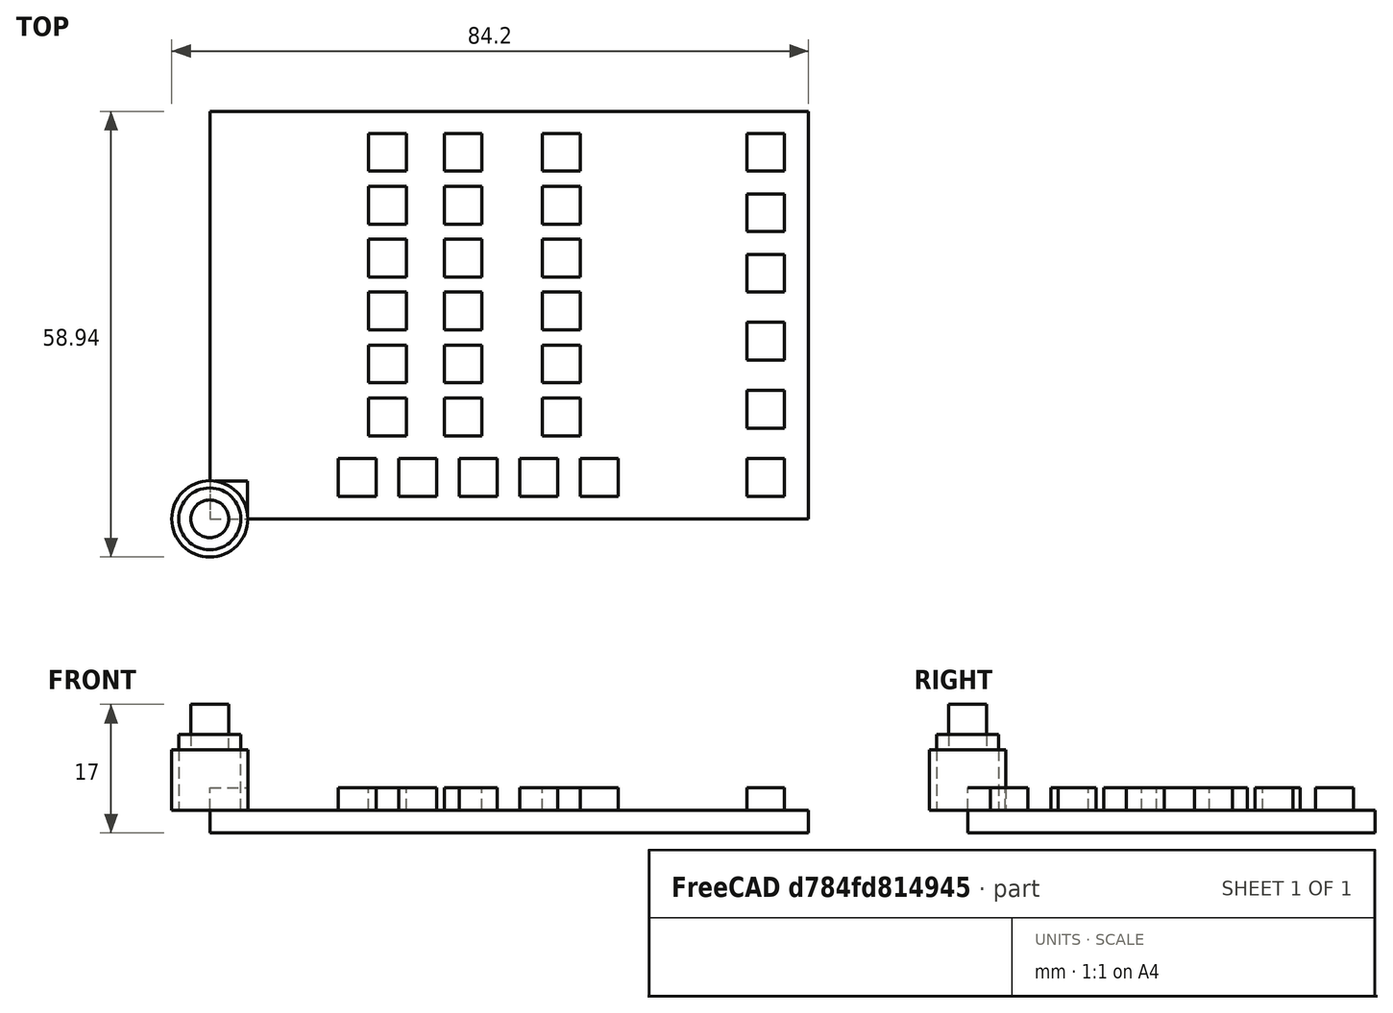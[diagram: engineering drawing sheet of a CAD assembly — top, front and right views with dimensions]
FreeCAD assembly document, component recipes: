
FREECAD ASSEMBLY — COMPONENT RECIPES ("PanelSchema")

This assembly document has 38 components, labeled P0..P37 below (a component is one placed body or linked part). 38 of them carry a construction recipe — the FreeCAD feature program that regenerates the part from scratch, quoted from this document or its linked companion documents; the rest are supplied as boundary geometry only. No exploded tour is included for this assembly.
COMPONENT P0 — recipe-attached ("Panel", modeled in this document).
Construction recipe (the document's own serialized feature program — sketch geometry with constraints, then the solid features built on it; lengths are millimeters unless a unit is written):

FEATURE [Sketcher::SketchObject] Sketch
  FullyConstrained = true
  MapMode = 5
  Support = -> [XY_Plane]
  sketch-geometry (4):
    g0: LineSegment StartX=0 StartY=0 StartZ=0 EndX=79.16 EndY=0 EndZ=0
    g1: LineSegment StartX=79.16 StartY=0 StartZ=0 EndX=79.16 EndY=53.9 EndZ=0
    g2: LineSegment StartX=79.16 StartY=53.9 StartZ=0 EndX=0 EndY=53.9 EndZ=0
    g3: LineSegment StartX=0 StartY=53.9 StartZ=0 EndX=0 EndY=0 EndZ=0
  constraints (11):
    c: Coincident(g0,g1)
    c: Coincident(g1,g2)
    c: Coincident(g2,g3)
    c: Coincident(g3,g0)
    c: Horizontal(g0)
    c: Horizontal(g2)
    c: Vertical(g1)
    c: Vertical(g3)
    c: Coincident(g0,g-1)
    c: DistanceX(g2,g2) = 79.16
    c: DistanceY(g3,g3) = 53.9
FEATURE [PartDesign::Pad] Pad
  Direction = (0,0,1)
  Length = 3
  Length2 = 10
  Profile = -> Sketch
  ReferenceAxis = -> Sketch [N_Axis]
  Type = 0
FEATURE [PartDesign::Body] Body  label="Panel"
  Group = -> [Sketch,Pad]
  Origin = -> Origin
  Tip = -> Pad
COMPONENT P1 — recipe-attached ("AP", modeled in this document).
Construction recipe (the document's own serialized feature program — sketch geometry with constraints, then the solid features built on it; lengths are millimeters unless a unit is written):

FEATURE [Sketcher::SketchObject] Sketch006
  FullyConstrained = true
  MapMode = 5
  Support = -> [XY_Plane004]
  sketch-geometry (4):
    g0: LineSegment StartX=0 StartY=0 StartZ=0 EndX=5 EndY=0 EndZ=0
    g1: LineSegment StartX=5 StartY=0 StartZ=0 EndX=5 EndY=5 EndZ=0
    g2: LineSegment StartX=5 StartY=5 StartZ=0 EndX=0 EndY=5 EndZ=0
    g3: LineSegment StartX=0 StartY=5 StartZ=0 EndX=0 EndY=0 EndZ=0
  constraints (11):
    c: Coincident(g0,g1)
    c: Coincident(g1,g2)
    c: Coincident(g2,g3)
    c: Coincident(g3,g0)
    c: Horizontal(g0)
    c: Horizontal(g2)
    c: Vertical(g1)
    c: Vertical(g3)
    c: Coincident(g0,g-1)
    c: DistanceY(g1,g1) = 5
    c: DistanceX(g2,g2) = 5
FEATURE [PartDesign::Pad] Pad005
  Direction = (0,0,1)
  Length = 3
  Length2 = 10
  Profile = -> Sketch006
  ReferenceAxis = -> Sketch006 [N_Axis]
  Type = 0
FEATURE [PartDesign::Body] Body004  label="AP"
  Group = -> [Sketch006,Pad005]
  Origin = -> Origin004
  Placement = pos=(21,46,3) rot=(0,0,1;0rad)
  Tip = -> Pad005
COMPONENT P2 — recipe-attached ("FD", modeled in this document).
Construction recipe (the document's own serialized feature program — sketch geometry with constraints, then the solid features built on it; lengths are millimeters unless a unit is written):

FEATURE [Sketcher::SketchObject] Sketch007
  FullyConstrained = true
  MapMode = 5
  Support = -> [XY_Plane005]
  sketch-geometry (4):
    g0: LineSegment StartX=0 StartY=0 StartZ=0 EndX=5 EndY=0 EndZ=0
    g1: LineSegment StartX=5 StartY=0 StartZ=0 EndX=5 EndY=5 EndZ=0
    g2: LineSegment StartX=5 StartY=5 StartZ=0 EndX=0 EndY=5 EndZ=0
    g3: LineSegment StartX=0 StartY=5 StartZ=0 EndX=0 EndY=0 EndZ=0
  constraints (11):
    c: Coincident(g0,g1)
    c: Coincident(g1,g2)
    c: Coincident(g2,g3)
    c: Coincident(g3,g0)
    c: Horizontal(g0)
    c: Horizontal(g2)
    c: Vertical(g1)
    c: Vertical(g3)
    c: Coincident(g0,g-1)
    c: DistanceY(g1,g1) = 5
    c: DistanceX(g2,g2) = 5
FEATURE [PartDesign::Pad] Pad006
  Direction = (0,0,1)
  Length = 3
  Length2 = 10
  Profile = -> Sketch007
  ReferenceAxis = -> Sketch007 [N_Axis]
  Type = 0
FEATURE [PartDesign::Body] Body005  label="FD"
  Group = -> [Sketch007,Pad006]
  Origin = -> Origin005
  Placement = pos=(21,39,3) rot=(0,0,1;0rad)
  Tip = -> Pad006
COMPONENT P3 — recipe-attached ("HDG", modeled in this document).
Construction recipe (the document's own serialized feature program — sketch geometry with constraints, then the solid features built on it; lengths are millimeters unless a unit is written):

FEATURE [Sketcher::SketchObject] Sketch008
  FullyConstrained = true
  MapMode = 5
  Support = -> [XY_Plane006]
  sketch-geometry (4):
    g0: LineSegment StartX=0 StartY=0 StartZ=0 EndX=5 EndY=0 EndZ=0
    g1: LineSegment StartX=5 StartY=0 StartZ=0 EndX=5 EndY=5 EndZ=0
    g2: LineSegment StartX=5 StartY=5 StartZ=0 EndX=0 EndY=5 EndZ=0
    g3: LineSegment StartX=0 StartY=5 StartZ=0 EndX=0 EndY=0 EndZ=0
  constraints (11):
    c: Coincident(g0,g1)
    c: Coincident(g1,g2)
    c: Coincident(g2,g3)
    c: Coincident(g3,g0)
    c: Horizontal(g0)
    c: Horizontal(g2)
    c: Vertical(g1)
    c: Vertical(g3)
    c: Coincident(g0,g-1)
    c: DistanceY(g1,g1) = 5
    c: DistanceX(g2,g2) = 5
FEATURE [PartDesign::Pad] Pad007
  Direction = (0,0,1)
  Length = 3
  Length2 = 10
  Profile = -> Sketch008
  ReferenceAxis = -> Sketch008 [N_Axis]
  Type = 0
FEATURE [PartDesign::Body] Body006  label="HDG"
  Group = -> [Sketch008,Pad007]
  Origin = -> Origin006
  Placement = pos=(21,32,3) rot=(0,0,1;0rad)
  Tip = -> Pad007
COMPONENT P4 — recipe-attached ("ALT", modeled in this document).
Construction recipe (the document's own serialized feature program — sketch geometry with constraints, then the solid features built on it; lengths are millimeters unless a unit is written):

FEATURE [Sketcher::SketchObject] Sketch009
  FullyConstrained = true
  MapMode = 5
  Support = -> [XY_Plane007]
  sketch-geometry (4):
    g0: LineSegment StartX=0 StartY=0 StartZ=0 EndX=5 EndY=0 EndZ=0
    g1: LineSegment StartX=5 StartY=0 StartZ=0 EndX=5 EndY=5 EndZ=0
    g2: LineSegment StartX=5 StartY=5 StartZ=0 EndX=0 EndY=5 EndZ=0
    g3: LineSegment StartX=0 StartY=5 StartZ=0 EndX=0 EndY=0 EndZ=0
  constraints (11):
    c: Coincident(g0,g1)
    c: Coincident(g1,g2)
    c: Coincident(g2,g3)
    c: Coincident(g3,g0)
    c: Horizontal(g0)
    c: Horizontal(g2)
    c: Vertical(g1)
    c: Vertical(g3)
    c: Coincident(g0,g-1)
    c: DistanceY(g1,g1) = 5
    c: DistanceX(g2,g2) = 5
FEATURE [PartDesign::Pad] Pad008
  Direction = (0,0,1)
  Length = 3
  Length2 = 10
  Profile = -> Sketch009
  ReferenceAxis = -> Sketch009 [N_Axis]
  Type = 0
FEATURE [PartDesign::Body] Body007  label="ALT"
  Group = -> [Sketch009,Pad008]
  Origin = -> Origin007
  Placement = pos=(21,25,3) rot=(0,0,1;0rad)
  Tip = -> Pad008
COMPONENT P5 — recipe-attached ("NAV", modeled in this document).
Construction recipe (the document's own serialized feature program — sketch geometry with constraints, then the solid features built on it; lengths are millimeters unless a unit is written):

FEATURE [Sketcher::SketchObject] Sketch010
  FullyConstrained = true
  MapMode = 5
  Support = -> [XY_Plane008]
  sketch-geometry (4):
    g0: LineSegment StartX=0 StartY=0 StartZ=0 EndX=5 EndY=0 EndZ=0
    g1: LineSegment StartX=5 StartY=0 StartZ=0 EndX=5 EndY=5 EndZ=0
    g2: LineSegment StartX=5 StartY=5 StartZ=0 EndX=0 EndY=5 EndZ=0
    g3: LineSegment StartX=0 StartY=5 StartZ=0 EndX=0 EndY=0 EndZ=0
  constraints (11):
    c: Coincident(g0,g1)
    c: Coincident(g1,g2)
    c: Coincident(g2,g3)
    c: Coincident(g3,g0)
    c: Horizontal(g0)
    c: Horizontal(g2)
    c: Vertical(g1)
    c: Vertical(g3)
    c: Coincident(g0,g-1)
    c: DistanceY(g1,g1) = 5
    c: DistanceX(g2,g2) = 5
FEATURE [PartDesign::Pad] Pad009
  Direction = (0,0,1)
  Length = 3
  Length2 = 10
  Profile = -> Sketch010
  ReferenceAxis = -> Sketch010 [N_Axis]
  Type = 0
FEATURE [PartDesign::Body] Body008  label="NAV"
  Group = -> [Sketch010,Pad009]
  Origin = -> Origin008
  Placement = pos=(21,18,3) rot=(0,0,1;0rad)
  Tip = -> Pad009
COMPONENT P6 — recipe-attached ("VNV", modeled in this document).
Construction recipe (the document's own serialized feature program — sketch geometry with constraints, then the solid features built on it; lengths are millimeters unless a unit is written):

FEATURE [Sketcher::SketchObject] Sketch011
  FullyConstrained = true
  MapMode = 5
  Support = -> [XY_Plane009]
  sketch-geometry (4):
    g0: LineSegment StartX=0 StartY=0 StartZ=0 EndX=5 EndY=0 EndZ=0
    g1: LineSegment StartX=5 StartY=0 StartZ=0 EndX=5 EndY=5 EndZ=0
    g2: LineSegment StartX=5 StartY=5 StartZ=0 EndX=0 EndY=5 EndZ=0
    g3: LineSegment StartX=0 StartY=5 StartZ=0 EndX=0 EndY=0 EndZ=0
  constraints (11):
    c: Coincident(g0,g1)
    c: Coincident(g1,g2)
    c: Coincident(g2,g3)
    c: Coincident(g3,g0)
    c: Horizontal(g0)
    c: Horizontal(g2)
    c: Vertical(g1)
    c: Vertical(g3)
    c: Coincident(g0,g-1)
    c: DistanceY(g1,g1) = 5
    c: DistanceX(g2,g2) = 5
FEATURE [PartDesign::Pad] Pad010
  Direction = (0,0,1)
  Length = 3
  Length2 = 10
  Profile = -> Sketch011
  ReferenceAxis = -> Sketch011 [N_Axis]
  Type = 0
FEATURE [PartDesign::Body] Body009  label="VNV"
  Group = -> [Sketch011,Pad010]
  Origin = -> Origin009
  Placement = pos=(21,11,3) rot=(0,0,1;0rad)
  Tip = -> Pad010
COMPONENT P7 — recipe-attached ("APR", modeled in this document).
Construction recipe (the document's own serialized feature program — sketch geometry with constraints, then the solid features built on it; lengths are millimeters unless a unit is written):

FEATURE [Sketcher::SketchObject] Sketch012
  FullyConstrained = true
  MapMode = 5
  Support = -> [XY_Plane010]
  sketch-geometry (4):
    g0: LineSegment StartX=0 StartY=0 StartZ=0 EndX=5 EndY=0 EndZ=0
    g1: LineSegment StartX=5 StartY=0 StartZ=0 EndX=5 EndY=5 EndZ=0
    g2: LineSegment StartX=5 StartY=5 StartZ=0 EndX=0 EndY=5 EndZ=0
    g3: LineSegment StartX=0 StartY=5 StartZ=0 EndX=0 EndY=0 EndZ=0
  constraints (11):
    c: Coincident(g0,g1)
    c: Coincident(g1,g2)
    c: Coincident(g2,g3)
    c: Coincident(g3,g0)
    c: Horizontal(g0)
    c: Horizontal(g2)
    c: Vertical(g1)
    c: Vertical(g3)
    c: Coincident(g0,g-1)
    c: DistanceY(g1,g1) = 5
    c: DistanceX(g2,g2) = 5
FEATURE [PartDesign::Pad] Pad011
  Direction = (0,0,1)
  Length = 3
  Length2 = 10
  Profile = -> Sketch012
  ReferenceAxis = -> Sketch012 [N_Axis]
  Type = 0
FEATURE [PartDesign::Body] Body010  label="APR"
  Group = -> [Sketch012,Pad011]
  Origin = -> Origin010
  Placement = pos=(31,46,3) rot=(0,0,1;0rad)
  Tip = -> Pad011
COMPONENT P8 — recipe-attached ("BC", modeled in this document).
Construction recipe (the document's own serialized feature program — sketch geometry with constraints, then the solid features built on it; lengths are millimeters unless a unit is written):

FEATURE [Sketcher::SketchObject] Sketch013
  FullyConstrained = true
  MapMode = 5
  Support = -> [XY_Plane011]
  sketch-geometry (4):
    g0: LineSegment StartX=0 StartY=0 StartZ=0 EndX=5 EndY=0 EndZ=0
    g1: LineSegment StartX=5 StartY=0 StartZ=0 EndX=5 EndY=5 EndZ=0
    g2: LineSegment StartX=5 StartY=5 StartZ=0 EndX=0 EndY=5 EndZ=0
    g3: LineSegment StartX=0 StartY=5 StartZ=0 EndX=0 EndY=0 EndZ=0
  constraints (11):
    c: Coincident(g0,g1)
    c: Coincident(g1,g2)
    c: Coincident(g2,g3)
    c: Coincident(g3,g0)
    c: Horizontal(g0)
    c: Horizontal(g2)
    c: Vertical(g1)
    c: Vertical(g3)
    c: Coincident(g0,g-1)
    c: DistanceY(g1,g1) = 5
    c: DistanceX(g2,g2) = 5
FEATURE [PartDesign::Pad] Pad012
  Direction = (0,0,1)
  Length = 3
  Length2 = 10
  Profile = -> Sketch013
  ReferenceAxis = -> Sketch013 [N_Axis]
  Type = 0
FEATURE [PartDesign::Body] Body011  label="BC"
  Group = -> [Sketch013,Pad012]
  Origin = -> Origin011
  Placement = pos=(31,39,3) rot=(0,0,1;0rad)
  Tip = -> Pad012
COMPONENT P9 — recipe-attached ("VS", modeled in this document).
Construction recipe (the document's own serialized feature program — sketch geometry with constraints, then the solid features built on it; lengths are millimeters unless a unit is written):

FEATURE [Sketcher::SketchObject] Sketch014
  FullyConstrained = true
  MapMode = 5
  Support = -> [XY_Plane012]
  sketch-geometry (4):
    g0: LineSegment StartX=0 StartY=0 StartZ=0 EndX=5 EndY=0 EndZ=0
    g1: LineSegment StartX=5 StartY=0 StartZ=0 EndX=5 EndY=5 EndZ=0
    g2: LineSegment StartX=5 StartY=5 StartZ=0 EndX=0 EndY=5 EndZ=0
    g3: LineSegment StartX=0 StartY=5 StartZ=0 EndX=0 EndY=0 EndZ=0
  constraints (11):
    c: Coincident(g0,g1)
    c: Coincident(g1,g2)
    c: Coincident(g2,g3)
    c: Coincident(g3,g0)
    c: Horizontal(g0)
    c: Horizontal(g2)
    c: Vertical(g1)
    c: Vertical(g3)
    c: Coincident(g0,g-1)
    c: DistanceY(g1,g1) = 5
    c: DistanceX(g2,g2) = 5
FEATURE [PartDesign::Pad] Pad013
  Direction = (0,0,1)
  Length = 3
  Length2 = 10
  Profile = -> Sketch014
  ReferenceAxis = -> Sketch014 [N_Axis]
  Type = 0
FEATURE [PartDesign::Body] Body012  label="VS"
  Group = -> [Sketch014,Pad013]
  Origin = -> Origin012
  Placement = pos=(31,32,3) rot=(0,0,1;0rad)
  Tip = -> Pad013
COMPONENT P10 — recipe-attached ("FLC", modeled in this document).
Construction recipe (the document's own serialized feature program — sketch geometry with constraints, then the solid features built on it; lengths are millimeters unless a unit is written):

FEATURE [Sketcher::SketchObject] Sketch015
  FullyConstrained = true
  MapMode = 5
  Support = -> [XY_Plane013]
  sketch-geometry (4):
    g0: LineSegment StartX=0 StartY=0 StartZ=0 EndX=5 EndY=0 EndZ=0
    g1: LineSegment StartX=5 StartY=0 StartZ=0 EndX=5 EndY=5 EndZ=0
    g2: LineSegment StartX=5 StartY=5 StartZ=0 EndX=0 EndY=5 EndZ=0
    g3: LineSegment StartX=0 StartY=5 StartZ=0 EndX=0 EndY=0 EndZ=0
  constraints (11):
    c: Coincident(g0,g1)
    c: Coincident(g1,g2)
    c: Coincident(g2,g3)
    c: Coincident(g3,g0)
    c: Horizontal(g0)
    c: Horizontal(g2)
    c: Vertical(g1)
    c: Vertical(g3)
    c: Coincident(g0,g-1)
    c: DistanceY(g1,g1) = 5
    c: DistanceX(g2,g2) = 5
FEATURE [PartDesign::Pad] Pad014
  Direction = (0,0,1)
  Length = 3
  Length2 = 10
  Profile = -> Sketch015
  ReferenceAxis = -> Sketch015 [N_Axis]
  Type = 0
FEATURE [PartDesign::Body] Body013  label="FLC"
  Group = -> [Sketch015,Pad014]
  Origin = -> Origin013
  Placement = pos=(31,25,3) rot=(0,0,1;0rad)
  Tip = -> Pad014
COMPONENT P11 — recipe-attached ("UP", modeled in this document).
Construction recipe (the document's own serialized feature program — sketch geometry with constraints, then the solid features built on it; lengths are millimeters unless a unit is written):

FEATURE [Sketcher::SketchObject] Sketch016
  FullyConstrained = true
  MapMode = 5
  Support = -> [XY_Plane014]
  sketch-geometry (4):
    g0: LineSegment StartX=0 StartY=0 StartZ=0 EndX=5 EndY=0 EndZ=0
    g1: LineSegment StartX=5 StartY=0 StartZ=0 EndX=5 EndY=5 EndZ=0
    g2: LineSegment StartX=5 StartY=5 StartZ=0 EndX=0 EndY=5 EndZ=0
    g3: LineSegment StartX=0 StartY=5 StartZ=0 EndX=0 EndY=0 EndZ=0
  constraints (11):
    c: Coincident(g0,g1)
    c: Coincident(g1,g2)
    c: Coincident(g2,g3)
    c: Coincident(g3,g0)
    c: Horizontal(g0)
    c: Horizontal(g2)
    c: Vertical(g1)
    c: Vertical(g3)
    c: Coincident(g0,g-1)
    c: DistanceY(g1,g1) = 5
    c: DistanceX(g2,g2) = 5
FEATURE [PartDesign::Pad] Pad015
  Direction = (0,0,1)
  Length = 3
  Length2 = 10
  Profile = -> Sketch016
  ReferenceAxis = -> Sketch016 [N_Axis]
  Type = 0
FEATURE [PartDesign::Body] Body014  label="UP"
  Group = -> [Sketch016,Pad015]
  Origin = -> Origin014
  Placement = pos=(31,18,3) rot=(0,0,1;0rad)
  Tip = -> Pad015
COMPONENT P12 — recipe-attached ("DN", modeled in this document).
Construction recipe (the document's own serialized feature program — sketch geometry with constraints, then the solid features built on it; lengths are millimeters unless a unit is written):

FEATURE [Sketcher::SketchObject] Sketch017
  FullyConstrained = true
  MapMode = 5
  Support = -> [XY_Plane015]
  sketch-geometry (4):
    g0: LineSegment StartX=0 StartY=0 StartZ=0 EndX=5 EndY=0 EndZ=0
    g1: LineSegment StartX=5 StartY=0 StartZ=0 EndX=5 EndY=5 EndZ=0
    g2: LineSegment StartX=5 StartY=5 StartZ=0 EndX=0 EndY=5 EndZ=0
    g3: LineSegment StartX=0 StartY=5 StartZ=0 EndX=0 EndY=0 EndZ=0
  constraints (11):
    c: Coincident(g0,g1)
    c: Coincident(g1,g2)
    c: Coincident(g2,g3)
    c: Coincident(g3,g0)
    c: Horizontal(g0)
    c: Horizontal(g2)
    c: Vertical(g1)
    c: Vertical(g3)
    c: Coincident(g0,g-1)
    c: DistanceY(g1,g1) = 5
    c: DistanceX(g2,g2) = 5
FEATURE [PartDesign::Pad] Pad016
  Direction = (0,0,1)
  Length = 3
  Length2 = 10
  Profile = -> Sketch017
  ReferenceAxis = -> Sketch017 [N_Axis]
  Type = 0
FEATURE [PartDesign::Body] Body015  label="DN"
  Group = -> [Sketch017,Pad016]
  Origin = -> Origin015
  Placement = pos=(31,11,3) rot=(0,0,1;0rad)
  Tip = -> Pad016
COMPONENT P13 — recipe-attached ("DCT", modeled in this document).
Construction recipe (the document's own serialized feature program — sketch geometry with constraints, then the solid features built on it; lengths are millimeters unless a unit is written):

FEATURE [Sketcher::SketchObject] Sketch018
  FullyConstrained = true
  MapMode = 5
  Support = -> [XY_Plane016]
  sketch-geometry (4):
    g0: LineSegment StartX=0 StartY=0 StartZ=0 EndX=5 EndY=0 EndZ=0
    g1: LineSegment StartX=5 StartY=0 StartZ=0 EndX=5 EndY=5 EndZ=0
    g2: LineSegment StartX=5 StartY=5 StartZ=0 EndX=0 EndY=5 EndZ=0
    g3: LineSegment StartX=0 StartY=5 StartZ=0 EndX=0 EndY=0 EndZ=0
  constraints (11):
    c: Coincident(g0,g1)
    c: Coincident(g1,g2)
    c: Coincident(g2,g3)
    c: Coincident(g3,g0)
    c: Horizontal(g0)
    c: Horizontal(g2)
    c: Vertical(g1)
    c: Vertical(g3)
    c: Coincident(g0,g-1)
    c: DistanceY(g1,g1) = 5
    c: DistanceX(g2,g2) = 5
FEATURE [PartDesign::Pad] Pad017
  Direction = (0,0,1)
  Length = 3
  Length2 = 10
  Profile = -> Sketch018
  ReferenceAxis = -> Sketch018 [N_Axis]
  Type = 0
FEATURE [PartDesign::Body] Body016  label="DCT"
  Group = -> [Sketch018,Pad017]
  Origin = -> Origin016
  Placement = pos=(44,46,3) rot=(0,0,1;0rad)
  Tip = -> Pad017
COMPONENT P14 — recipe-attached ("MNU", modeled in this document).
Construction recipe (the document's own serialized feature program — sketch geometry with constraints, then the solid features built on it; lengths are millimeters unless a unit is written):

FEATURE [Sketcher::SketchObject] Sketch019
  FullyConstrained = true
  MapMode = 5
  Support = -> [XY_Plane017]
  sketch-geometry (4):
    g0: LineSegment StartX=0 StartY=0 StartZ=0 EndX=5 EndY=0 EndZ=0
    g1: LineSegment StartX=5 StartY=0 StartZ=0 EndX=5 EndY=5 EndZ=0
    g2: LineSegment StartX=5 StartY=5 StartZ=0 EndX=0 EndY=5 EndZ=0
    g3: LineSegment StartX=0 StartY=5 StartZ=0 EndX=0 EndY=0 EndZ=0
  constraints (11):
    c: Coincident(g0,g1)
    c: Coincident(g1,g2)
    c: Coincident(g2,g3)
    c: Coincident(g3,g0)
    c: Horizontal(g0)
    c: Horizontal(g2)
    c: Vertical(g1)
    c: Vertical(g3)
    c: Coincident(g0,g-1)
    c: DistanceY(g1,g1) = 5
    c: DistanceX(g2,g2) = 5
FEATURE [PartDesign::Pad] Pad018
  Direction = (0,0,1)
  Length = 3
  Length2 = 10
  Profile = -> Sketch019
  ReferenceAxis = -> Sketch019 [N_Axis]
  Type = 0
FEATURE [PartDesign::Body] Body017  label="MNU"
  Group = -> [Sketch019,Pad018]
  Origin = -> Origin017
  Placement = pos=(44,39,3) rot=(0,0,1;0rad)
  Tip = -> Pad018
COMPONENT P15 — recipe-attached ("FPL", modeled in this document).
Construction recipe (the document's own serialized feature program — sketch geometry with constraints, then the solid features built on it; lengths are millimeters unless a unit is written):

FEATURE [Sketcher::SketchObject] Sketch020
  FullyConstrained = true
  MapMode = 5
  Support = -> [XY_Plane018]
  sketch-geometry (4):
    g0: LineSegment StartX=0 StartY=0 StartZ=0 EndX=5 EndY=0 EndZ=0
    g1: LineSegment StartX=5 StartY=0 StartZ=0 EndX=5 EndY=5 EndZ=0
    g2: LineSegment StartX=5 StartY=5 StartZ=0 EndX=0 EndY=5 EndZ=0
    g3: LineSegment StartX=0 StartY=5 StartZ=0 EndX=0 EndY=0 EndZ=0
  constraints (11):
    c: Coincident(g0,g1)
    c: Coincident(g1,g2)
    c: Coincident(g2,g3)
    c: Coincident(g3,g0)
    c: Horizontal(g0)
    c: Horizontal(g2)
    c: Vertical(g1)
    c: Vertical(g3)
    c: Coincident(g0,g-1)
    c: DistanceY(g1,g1) = 5
    c: DistanceX(g2,g2) = 5
FEATURE [PartDesign::Pad] Pad019
  Direction = (0,0,1)
  Length = 3
  Length2 = 10
  Profile = -> Sketch020
  ReferenceAxis = -> Sketch020 [N_Axis]
  Type = 0
FEATURE [PartDesign::Body] Body018  label="FPL"
  Group = -> [Sketch020,Pad019]
  Origin = -> Origin018
  Placement = pos=(44,32,3) rot=(0,0,1;0rad)
  Tip = -> Pad019
COMPONENT P16 — recipe-attached ("PROC", modeled in this document).
Construction recipe (the document's own serialized feature program — sketch geometry with constraints, then the solid features built on it; lengths are millimeters unless a unit is written):

FEATURE [Sketcher::SketchObject] Sketch021
  FullyConstrained = true
  MapMode = 5
  Support = -> [XY_Plane019]
  sketch-geometry (4):
    g0: LineSegment StartX=0 StartY=0 StartZ=0 EndX=5 EndY=0 EndZ=0
    g1: LineSegment StartX=5 StartY=0 StartZ=0 EndX=5 EndY=5 EndZ=0
    g2: LineSegment StartX=5 StartY=5 StartZ=0 EndX=0 EndY=5 EndZ=0
    g3: LineSegment StartX=0 StartY=5 StartZ=0 EndX=0 EndY=0 EndZ=0
  constraints (11):
    c: Coincident(g0,g1)
    c: Coincident(g1,g2)
    c: Coincident(g2,g3)
    c: Coincident(g3,g0)
    c: Horizontal(g0)
    c: Horizontal(g2)
    c: Vertical(g1)
    c: Vertical(g3)
    c: Coincident(g0,g-1)
    c: DistanceY(g1,g1) = 5
    c: DistanceX(g2,g2) = 5
FEATURE [PartDesign::Pad] Pad020
  Direction = (0,0,1)
  Length = 3
  Length2 = 10
  Profile = -> Sketch021
  ReferenceAxis = -> Sketch021 [N_Axis]
  Type = 0
FEATURE [PartDesign::Body] Body019  label="PROC"
  Group = -> [Sketch021,Pad020]
  Origin = -> Origin019
  Placement = pos=(44,25,3) rot=(0,0,1;0rad)
  Tip = -> Pad020
COMPONENT P17 — recipe-attached ("CLR", modeled in this document).
Construction recipe (the document's own serialized feature program — sketch geometry with constraints, then the solid features built on it; lengths are millimeters unless a unit is written):

FEATURE [Sketcher::SketchObject] Sketch022
  FullyConstrained = true
  MapMode = 5
  Support = -> [XY_Plane020]
  sketch-geometry (4):
    g0: LineSegment StartX=0 StartY=0 StartZ=0 EndX=5 EndY=0 EndZ=0
    g1: LineSegment StartX=5 StartY=0 StartZ=0 EndX=5 EndY=5 EndZ=0
    g2: LineSegment StartX=5 StartY=5 StartZ=0 EndX=0 EndY=5 EndZ=0
    g3: LineSegment StartX=0 StartY=5 StartZ=0 EndX=0 EndY=0 EndZ=0
  constraints (11):
    c: Coincident(g0,g1)
    c: Coincident(g1,g2)
    c: Coincident(g2,g3)
    c: Coincident(g3,g0)
    c: Horizontal(g0)
    c: Horizontal(g2)
    c: Vertical(g1)
    c: Vertical(g3)
    c: Coincident(g0,g-1)
    c: DistanceY(g1,g1) = 5
    c: DistanceX(g2,g2) = 5
FEATURE [PartDesign::Pad] Pad021
  Direction = (0,0,1)
  Length = 3
  Length2 = 10
  Profile = -> Sketch022
  ReferenceAxis = -> Sketch022 [N_Axis]
  Type = 0
FEATURE [PartDesign::Body] Body020  label="CLR"
  Group = -> [Sketch022,Pad021]
  Origin = -> Origin020
  Placement = pos=(44,18,3) rot=(0,0,1;0rad)
  Tip = -> Pad021
COMPONENT P18 — recipe-attached ("ENT", modeled in this document).
Construction recipe (the document's own serialized feature program — sketch geometry with constraints, then the solid features built on it; lengths are millimeters unless a unit is written):

FEATURE [Sketcher::SketchObject] Sketch023
  FullyConstrained = true
  MapMode = 5
  Support = -> [XY_Plane021]
  sketch-geometry (4):
    g0: LineSegment StartX=0 StartY=0 StartZ=0 EndX=5 EndY=0 EndZ=0
    g1: LineSegment StartX=5 StartY=0 StartZ=0 EndX=5 EndY=5 EndZ=0
    g2: LineSegment StartX=5 StartY=5 StartZ=0 EndX=0 EndY=5 EndZ=0
    g3: LineSegment StartX=0 StartY=5 StartZ=0 EndX=0 EndY=0 EndZ=0
  constraints (11):
    c: Coincident(g0,g1)
    c: Coincident(g1,g2)
    c: Coincident(g2,g3)
    c: Coincident(g3,g0)
    c: Horizontal(g0)
    c: Horizontal(g2)
    c: Vertical(g1)
    c: Vertical(g3)
    c: Coincident(g0,g-1)
    c: DistanceY(g1,g1) = 5
    c: DistanceX(g2,g2) = 5
FEATURE [PartDesign::Pad] Pad022
  Direction = (0,0,1)
  Length = 3
  Length2 = 10
  Profile = -> Sketch023
  ReferenceAxis = -> Sketch023 [N_Axis]
  Type = 0
FEATURE [PartDesign::Body] Body021  label="ENT"
  Group = -> [Sketch023,Pad022]
  Origin = -> Origin021
  Placement = pos=(44,11,3) rot=(0,0,1;0rad)
  Tip = -> Pad022
COMPONENT P19 — recipe-attached ("SW1", modeled in this document).
Construction recipe (the document's own serialized feature program — sketch geometry with constraints, then the solid features built on it; lengths are millimeters unless a unit is written):

FEATURE [Sketcher::SketchObject] Sketch024
  FullyConstrained = true
  MapMode = 5
  Support = -> [XY_Plane022]
  sketch-geometry (4):
    g0: LineSegment StartX=0 StartY=0 StartZ=0 EndX=5 EndY=0 EndZ=0
    g1: LineSegment StartX=5 StartY=0 StartZ=0 EndX=5 EndY=5 EndZ=0
    g2: LineSegment StartX=5 StartY=5 StartZ=0 EndX=0 EndY=5 EndZ=0
    g3: LineSegment StartX=0 StartY=5 StartZ=0 EndX=0 EndY=0 EndZ=0
  constraints (11):
    c: Coincident(g0,g1)
    c: Coincident(g1,g2)
    c: Coincident(g2,g3)
    c: Coincident(g3,g0)
    c: Horizontal(g0)
    c: Horizontal(g2)
    c: Vertical(g1)
    c: Vertical(g3)
    c: Coincident(g0,g-1)
    c: DistanceY(g1,g1) = 5
    c: DistanceX(g2,g2) = 5
FEATURE [PartDesign::Pad] Pad023
  Direction = (0,0,1)
  Length = 3
  Length2 = 10
  Profile = -> Sketch024
  ReferenceAxis = -> Sketch024 [N_Axis]
  Type = 0
FEATURE [PartDesign::Body] Body022  label="SW1"
  Group = -> [Sketch024,Pad023]
  Origin = -> Origin022
  Placement = pos=(17,3,3) rot=(0,0,1;0rad)
  Tip = -> Pad023
COMPONENT P20 — recipe-attached ("SW2", modeled in this document).
Construction recipe (the document's own serialized feature program — sketch geometry with constraints, then the solid features built on it; lengths are millimeters unless a unit is written):

FEATURE [Sketcher::SketchObject] Sketch025
  FullyConstrained = true
  MapMode = 5
  Support = -> [XY_Plane023]
  sketch-geometry (4):
    g0: LineSegment StartX=0 StartY=0 StartZ=0 EndX=5 EndY=0 EndZ=0
    g1: LineSegment StartX=5 StartY=0 StartZ=0 EndX=5 EndY=5 EndZ=0
    g2: LineSegment StartX=5 StartY=5 StartZ=0 EndX=0 EndY=5 EndZ=0
    g3: LineSegment StartX=0 StartY=5 StartZ=0 EndX=0 EndY=0 EndZ=0
  constraints (11):
    c: Coincident(g0,g1)
    c: Coincident(g1,g2)
    c: Coincident(g2,g3)
    c: Coincident(g3,g0)
    c: Horizontal(g0)
    c: Horizontal(g2)
    c: Vertical(g1)
    c: Vertical(g3)
    c: Coincident(g0,g-1)
    c: DistanceY(g1,g1) = 5
    c: DistanceX(g2,g2) = 5
FEATURE [PartDesign::Pad] Pad024
  Direction = (0,0,1)
  Length = 3
  Length2 = 10
  Profile = -> Sketch025
  ReferenceAxis = -> Sketch025 [N_Axis]
  Type = 0
FEATURE [PartDesign::Body] Body023  label="SW2"
  Group = -> [Sketch025,Pad024]
  Origin = -> Origin023
  Placement = pos=(25,3,3) rot=(0,0,1;0rad)
  Tip = -> Pad024
COMPONENT P21 — recipe-attached ("SW3", modeled in this document).
Construction recipe (the document's own serialized feature program — sketch geometry with constraints, then the solid features built on it; lengths are millimeters unless a unit is written):

FEATURE [Sketcher::SketchObject] Sketch026
  FullyConstrained = true
  MapMode = 5
  Support = -> [XY_Plane024]
  sketch-geometry (4):
    g0: LineSegment StartX=0 StartY=0 StartZ=0 EndX=5 EndY=0 EndZ=0
    g1: LineSegment StartX=5 StartY=0 StartZ=0 EndX=5 EndY=5 EndZ=0
    g2: LineSegment StartX=5 StartY=5 StartZ=0 EndX=0 EndY=5 EndZ=0
    g3: LineSegment StartX=0 StartY=5 StartZ=0 EndX=0 EndY=0 EndZ=0
  constraints (11):
    c: Coincident(g0,g1)
    c: Coincident(g1,g2)
    c: Coincident(g2,g3)
    c: Coincident(g3,g0)
    c: Horizontal(g0)
    c: Horizontal(g2)
    c: Vertical(g1)
    c: Vertical(g3)
    c: Coincident(g0,g-1)
    c: DistanceY(g1,g1) = 5
    c: DistanceX(g2,g2) = 5
FEATURE [PartDesign::Pad] Pad025
  Direction = (0,0,1)
  Length = 3
  Length2 = 10
  Profile = -> Sketch026
  ReferenceAxis = -> Sketch026 [N_Axis]
  Type = 0
FEATURE [PartDesign::Body] Body024  label="SW3"
  Group = -> [Sketch026,Pad025]
  Origin = -> Origin024
  Placement = pos=(33,3,3) rot=(0,0,1;0rad)
  Tip = -> Pad025
COMPONENT P22 — recipe-attached ("SW4", modeled in this document).
Construction recipe (the document's own serialized feature program — sketch geometry with constraints, then the solid features built on it; lengths are millimeters unless a unit is written):

FEATURE [Sketcher::SketchObject] Sketch027
  FullyConstrained = true
  MapMode = 5
  Support = -> [XY_Plane025]
  sketch-geometry (4):
    g0: LineSegment StartX=0 StartY=0 StartZ=0 EndX=5 EndY=0 EndZ=0
    g1: LineSegment StartX=5 StartY=0 StartZ=0 EndX=5 EndY=5 EndZ=0
    g2: LineSegment StartX=5 StartY=5 StartZ=0 EndX=0 EndY=5 EndZ=0
    g3: LineSegment StartX=0 StartY=5 StartZ=0 EndX=0 EndY=0 EndZ=0
  constraints (11):
    c: Coincident(g0,g1)
    c: Coincident(g1,g2)
    c: Coincident(g2,g3)
    c: Coincident(g3,g0)
    c: Horizontal(g0)
    c: Horizontal(g2)
    c: Vertical(g1)
    c: Vertical(g3)
    c: Coincident(g0,g-1)
    c: DistanceY(g1,g1) = 5
    c: DistanceX(g2,g2) = 5
FEATURE [PartDesign::Pad] Pad026
  Direction = (0,0,1)
  Length = 3
  Length2 = 10
  Profile = -> Sketch027
  ReferenceAxis = -> Sketch027 [N_Axis]
  Type = 0
FEATURE [PartDesign::Body] Body025  label="SW4"
  Group = -> [Sketch027,Pad026]
  Origin = -> Origin025
  Placement = pos=(41,3,3) rot=(0,0,1;0rad)
  Tip = -> Pad026
COMPONENT P23 — recipe-attached ("SW5", modeled in this document).
Construction recipe (the document's own serialized feature program — sketch geometry with constraints, then the solid features built on it; lengths are millimeters unless a unit is written):

FEATURE [Sketcher::SketchObject] Sketch028
  FullyConstrained = true
  MapMode = 5
  Support = -> [XY_Plane026]
  sketch-geometry (4):
    g0: LineSegment StartX=0 StartY=0 StartZ=0 EndX=5 EndY=0 EndZ=0
    g1: LineSegment StartX=5 StartY=0 StartZ=0 EndX=5 EndY=5 EndZ=0
    g2: LineSegment StartX=5 StartY=5 StartZ=0 EndX=0 EndY=5 EndZ=0
    g3: LineSegment StartX=0 StartY=5 StartZ=0 EndX=0 EndY=0 EndZ=0
  constraints (11):
    c: Coincident(g0,g1)
    c: Coincident(g1,g2)
    c: Coincident(g2,g3)
    c: Coincident(g3,g0)
    c: Horizontal(g0)
    c: Horizontal(g2)
    c: Vertical(g1)
    c: Vertical(g3)
    c: Coincident(g0,g-1)
    c: DistanceY(g1,g1) = 5
    c: DistanceX(g2,g2) = 5
FEATURE [PartDesign::Pad] Pad027
  Direction = (0,0,1)
  Length = 3
  Length2 = 10
  Profile = -> Sketch028
  ReferenceAxis = -> Sketch028 [N_Axis]
  Type = 0
FEATURE [PartDesign::Body] Body026  label="SW5"
  Group = -> [Sketch028,Pad027]
  Origin = -> Origin026
  Placement = pos=(49,3,3) rot=(0,0,1;0rad)
  Tip = -> Pad027
COMPONENT P24 — recipe-attached ("SW6", modeled in this document).
Construction recipe (the document's own serialized feature program — sketch geometry with constraints, then the solid features built on it; lengths are millimeters unless a unit is written):

FEATURE [Sketcher::SketchObject] Sketch029
  FullyConstrained = true
  MapMode = 5
  Support = -> [XY_Plane027]
  sketch-geometry (4):
    g0: LineSegment StartX=0 StartY=0 StartZ=0 EndX=5 EndY=0 EndZ=0
    g1: LineSegment StartX=5 StartY=0 StartZ=0 EndX=5 EndY=5 EndZ=0
    g2: LineSegment StartX=5 StartY=5 StartZ=0 EndX=0 EndY=5 EndZ=0
    g3: LineSegment StartX=0 StartY=5 StartZ=0 EndX=0 EndY=0 EndZ=0
  constraints (11):
    c: Coincident(g0,g1)
    c: Coincident(g1,g2)
    c: Coincident(g2,g3)
    c: Coincident(g3,g0)
    c: Horizontal(g0)
    c: Horizontal(g2)
    c: Vertical(g1)
    c: Vertical(g3)
    c: Coincident(g0,g-1)
    c: DistanceY(g1,g1) = 5
    c: DistanceX(g2,g2) = 5
FEATURE [PartDesign::Pad] Pad028
  Direction = (0,0,1)
  Length = 3
  Length2 = 10
  Profile = -> Sketch029
  ReferenceAxis = -> Sketch029 [N_Axis]
  Type = 0
FEATURE [PartDesign::Body] Body027  label="SW6"
  Group = -> [Sketch029,Pad028]
  Origin = -> Origin027
  Placement = pos=(71,3,3) rot=(0,0,1;0rad)
  Tip = -> Pad028
COMPONENT P25 — recipe-attached ("SW7", modeled in this document).
Construction recipe (the document's own serialized feature program — sketch geometry with constraints, then the solid features built on it; lengths are millimeters unless a unit is written):

FEATURE [Sketcher::SketchObject] Sketch030
  FullyConstrained = true
  MapMode = 5
  Support = -> [XY_Plane028]
  sketch-geometry (4):
    g0: LineSegment StartX=0 StartY=0 StartZ=0 EndX=5 EndY=0 EndZ=0
    g1: LineSegment StartX=5 StartY=0 StartZ=0 EndX=5 EndY=5 EndZ=0
    g2: LineSegment StartX=5 StartY=5 StartZ=0 EndX=0 EndY=5 EndZ=0
    g3: LineSegment StartX=0 StartY=5 StartZ=0 EndX=0 EndY=0 EndZ=0
  constraints (11):
    c: Coincident(g0,g1)
    c: Coincident(g1,g2)
    c: Coincident(g2,g3)
    c: Coincident(g3,g0)
    c: Horizontal(g0)
    c: Horizontal(g2)
    c: Vertical(g1)
    c: Vertical(g3)
    c: Coincident(g0,g-1)
    c: DistanceY(g1,g1) = 5
    c: DistanceX(g2,g2) = 5
FEATURE [PartDesign::Pad] Pad029
  Direction = (0,0,1)
  Length = 3
  Length2 = 10
  Profile = -> Sketch030
  ReferenceAxis = -> Sketch030 [N_Axis]
  Type = 0
FEATURE [PartDesign::Body] Body028  label="SW7"
  Group = -> [Sketch030,Pad029]
  Origin = -> Origin028
  Placement = pos=(71,12,3) rot=(0,0,1;0rad)
  Tip = -> Pad029
COMPONENT P26 — recipe-attached ("SW8", modeled in this document).
Construction recipe (the document's own serialized feature program — sketch geometry with constraints, then the solid features built on it; lengths are millimeters unless a unit is written):

FEATURE [Sketcher::SketchObject] Sketch031
  FullyConstrained = true
  MapMode = 5
  Support = -> [XY_Plane029]
  sketch-geometry (4):
    g0: LineSegment StartX=0 StartY=0 StartZ=0 EndX=5 EndY=0 EndZ=0
    g1: LineSegment StartX=5 StartY=0 StartZ=0 EndX=5 EndY=5 EndZ=0
    g2: LineSegment StartX=5 StartY=5 StartZ=0 EndX=0 EndY=5 EndZ=0
    g3: LineSegment StartX=0 StartY=5 StartZ=0 EndX=0 EndY=0 EndZ=0
  constraints (11):
    c: Coincident(g0,g1)
    c: Coincident(g1,g2)
    c: Coincident(g2,g3)
    c: Coincident(g3,g0)
    c: Horizontal(g0)
    c: Horizontal(g2)
    c: Vertical(g1)
    c: Vertical(g3)
    c: Coincident(g0,g-1)
    c: DistanceY(g1,g1) = 5
    c: DistanceX(g2,g2) = 5
FEATURE [PartDesign::Pad] Pad030
  Direction = (0,0,1)
  Length = 3
  Length2 = 10
  Profile = -> Sketch031
  ReferenceAxis = -> Sketch031 [N_Axis]
  Type = 0
FEATURE [PartDesign::Body] Body029  label="SW8"
  Group = -> [Sketch031,Pad030]
  Origin = -> Origin029
  Placement = pos=(71,21,3) rot=(0,0,1;0rad)
  Tip = -> Pad030
COMPONENT P27 — recipe-attached ("SW9", modeled in this document).
Construction recipe (the document's own serialized feature program — sketch geometry with constraints, then the solid features built on it; lengths are millimeters unless a unit is written):

FEATURE [Sketcher::SketchObject] Sketch032
  FullyConstrained = true
  MapMode = 5
  Support = -> [XY_Plane030]
  sketch-geometry (4):
    g0: LineSegment StartX=0 StartY=0 StartZ=0 EndX=5 EndY=0 EndZ=0
    g1: LineSegment StartX=5 StartY=0 StartZ=0 EndX=5 EndY=5 EndZ=0
    g2: LineSegment StartX=5 StartY=5 StartZ=0 EndX=0 EndY=5 EndZ=0
    g3: LineSegment StartX=0 StartY=5 StartZ=0 EndX=0 EndY=0 EndZ=0
  constraints (11):
    c: Coincident(g0,g1)
    c: Coincident(g1,g2)
    c: Coincident(g2,g3)
    c: Coincident(g3,g0)
    c: Horizontal(g0)
    c: Horizontal(g2)
    c: Vertical(g1)
    c: Vertical(g3)
    c: Coincident(g0,g-1)
    c: DistanceY(g1,g1) = 5
    c: DistanceX(g2,g2) = 5
FEATURE [PartDesign::Pad] Pad031
  Direction = (0,0,1)
  Length = 3
  Length2 = 10
  Profile = -> Sketch032
  ReferenceAxis = -> Sketch032 [N_Axis]
  Type = 0
FEATURE [PartDesign::Body] Body030  label="SW9"
  Group = -> [Sketch032,Pad031]
  Origin = -> Origin030
  Placement = pos=(71,30,3) rot=(0,0,1;0rad)
  Tip = -> Pad031
COMPONENT P28 — recipe-attached ("SW10", modeled in this document).
Construction recipe (the document's own serialized feature program — sketch geometry with constraints, then the solid features built on it; lengths are millimeters unless a unit is written):

FEATURE [Sketcher::SketchObject] Sketch033
  FullyConstrained = true
  MapMode = 5
  Support = -> [XY_Plane031]
  sketch-geometry (4):
    g0: LineSegment StartX=0 StartY=0 StartZ=0 EndX=5 EndY=0 EndZ=0
    g1: LineSegment StartX=5 StartY=0 StartZ=0 EndX=5 EndY=5 EndZ=0
    g2: LineSegment StartX=5 StartY=5 StartZ=0 EndX=0 EndY=5 EndZ=0
    g3: LineSegment StartX=0 StartY=5 StartZ=0 EndX=0 EndY=0 EndZ=0
  constraints (11):
    c: Coincident(g0,g1)
    c: Coincident(g1,g2)
    c: Coincident(g2,g3)
    c: Coincident(g3,g0)
    c: Horizontal(g0)
    c: Horizontal(g2)
    c: Vertical(g1)
    c: Vertical(g3)
    c: Coincident(g0,g-1)
    c: DistanceY(g1,g1) = 5
    c: DistanceX(g2,g2) = 5
FEATURE [PartDesign::Pad] Pad032
  Direction = (0,0,1)
  Length = 3
  Length2 = 10
  Profile = -> Sketch033
  ReferenceAxis = -> Sketch033 [N_Axis]
  Type = 0
FEATURE [PartDesign::Body] Body031  label="SW10"
  Group = -> [Sketch033,Pad032]
  Origin = -> Origin031
  Placement = pos=(71,38,3) rot=(0,0,1;0rad)
  Tip = -> Pad032
COMPONENT P29 — recipe-attached ("SW11", modeled in this document).
Construction recipe (the document's own serialized feature program — sketch geometry with constraints, then the solid features built on it; lengths are millimeters unless a unit is written):

FEATURE [Sketcher::SketchObject] Sketch034
  FullyConstrained = true
  MapMode = 5
  Support = -> [XY_Plane032]
  sketch-geometry (4):
    g0: LineSegment StartX=0 StartY=0 StartZ=0 EndX=5 EndY=0 EndZ=0
    g1: LineSegment StartX=5 StartY=0 StartZ=0 EndX=5 EndY=5 EndZ=0
    g2: LineSegment StartX=5 StartY=5 StartZ=0 EndX=0 EndY=5 EndZ=0
    g3: LineSegment StartX=0 StartY=5 StartZ=0 EndX=0 EndY=0 EndZ=0
  constraints (11):
    c: Coincident(g0,g1)
    c: Coincident(g1,g2)
    c: Coincident(g2,g3)
    c: Coincident(g3,g0)
    c: Horizontal(g0)
    c: Horizontal(g2)
    c: Vertical(g1)
    c: Vertical(g3)
    c: Coincident(g0,g-1)
    c: DistanceY(g1,g1) = 5
    c: DistanceX(g2,g2) = 5
FEATURE [PartDesign::Pad] Pad033
  Direction = (0,0,1)
  Length = 3
  Length2 = 10
  Profile = -> Sketch034
  ReferenceAxis = -> Sketch034 [N_Axis]
  Type = 0
FEATURE [PartDesign::Body] Body032  label="SW11"
  Group = -> [Sketch034,Pad033]
  Origin = -> Origin032
  Placement = pos=(71,46,3) rot=(0,0,1;0rad)
  Tip = -> Pad033
COMPONENT P30 — recipe-attached ("NAV-Encoder", modeled in this document).
Construction recipe (the document's own serialized feature program — sketch geometry with constraints, then the solid features built on it; lengths are millimeters unless a unit is written):

FEATURE [Sketcher::SketchObject] Sketch003
  FullyConstrained = true
  MapMode = 5
  Support = -> [XY_Plane002]
  sketch-geometry (1):
    g0: Circle CenterX=0 CenterY=0 CenterZ=0 NormalX=0 NormalY=0 NormalZ=1 AngleXU=0 Radius=5.04
  constraints (2):
    c: Coincident(g0,g-1)
    c: Radius(g0) = 5.04
FEATURE [PartDesign::Pad] Pad002
  Direction = (0,0,1)
  Length = 8
  Length2 = 10
  Profile = -> Sketch003
  ReferenceAxis = -> Sketch003 [N_Axis]
  Type = 0
FEATURE [Sketcher::SketchObject] Sketch004
  FullyConstrained = true
  MapMode = 5
  Placement = pos=(0,0,8) rot=(0,0,1;0rad)
  Support = -> [Pad002]
  sketch-geometry (1):
    g0: Circle CenterX=0 CenterY=0 CenterZ=0 NormalX=0 NormalY=0 NormalZ=1 AngleXU=0 Radius=2.5
  constraints (2):
    c: Coincident(g0,g-1)
    c: Radius(g0) = 2.5
FEATURE [PartDesign::Pad] Pad003
  BaseFeature = -> Pad002
  Direction = (0,0,1)
  Length = 6
  Length2 = 10
  Profile = -> Sketch004
  ReferenceAxis = -> Sketch004 [N_Axis]
  Type = 0
FEATURE [PartDesign::Body] Body002  label="DoubleEncoder"
  Group = -> [Sketch003,Pad002,Sketch004,Pad003]
  Origin = -> Origin002
  Placement = pos=(0,0,3) rot=(0,0,1;0rad)
  Tip = -> Pad003
COMPONENT P31 — recipe-attached ("NAV-Switch", modeled in this document).
Construction recipe (the document's own serialized feature program — sketch geometry with constraints, then the solid features built on it; lengths are millimeters unless a unit is written):

FEATURE [Sketcher::SketchObject] Sketch005
  FullyConstrained = true
  MapMode = 5
  Support = -> [XY_Plane003]
  sketch-geometry (4):
    g0: LineSegment StartX=0 StartY=0 StartZ=0 EndX=5 EndY=0 EndZ=0
    g1: LineSegment StartX=5 StartY=0 StartZ=0 EndX=5 EndY=5 EndZ=0
    g2: LineSegment StartX=5 StartY=5 StartZ=0 EndX=0 EndY=5 EndZ=0
    g3: LineSegment StartX=0 StartY=5 StartZ=0 EndX=0 EndY=0 EndZ=0
  constraints (11):
    c: Coincident(g0,g1)
    c: Coincident(g1,g2)
    c: Coincident(g2,g3)
    c: Coincident(g3,g0)
    c: Horizontal(g0)
    c: Horizontal(g2)
    c: Vertical(g1)
    c: Vertical(g3)
    c: Coincident(g0,g-1)
    c: DistanceY(g1,g1) = 5
    c: DistanceX(g2,g2) = 5
FEATURE [PartDesign::Pad] Pad004
  Direction = (0,0,1)
  Length = 3
  Length2 = 10
  Profile = -> Sketch005
  ReferenceAxis = -> Sketch005 [N_Axis]
  Type = 0
FEATURE [PartDesign::Body] Body003  label="PushButton"
  Group = -> [Sketch005,Pad004]
  Origin = -> Origin003
  Placement = pos=(0,0,3) rot=(0,0,1;0rad)
  Tip = -> Pad004
COMPONENT P32 — same part as P30; its construction recipe is shown at P30.
COMPONENT P33 — same part as P31; its construction recipe is shown at P31.
COMPONENT P34 — recipe-attached ("HDG-Encoder", modeled in this document).
Construction recipe (the document's own serialized feature program — sketch geometry with constraints, then the solid features built on it; lengths are millimeters unless a unit is written):

FEATURE [Sketcher::SketchObject] Sketch002
  FullyConstrained = true
  MapMode = 5
  Support = -> [XY_Plane001]
  sketch-geometry (1):
    g0: Circle CenterX=0 CenterY=0 CenterZ=0 NormalX=0 NormalY=0 NormalZ=1 AngleXU=0 Radius=4.1
  constraints (2):
    c: Radius(g0) = 4.1
    c: Coincident(g-1,g0)
FEATURE [PartDesign::Pad] Pad001
  Direction = (0,0,1)
  Length = 10
  Length2 = 10
  Profile = -> Sketch002
  ReferenceAxis = -> Sketch002 [N_Axis]
  Type = 0
FEATURE [PartDesign::Body] Body001  label="SingleEncoder"
  Group = -> [Sketch002,Pad001]
  Origin = -> Origin001
  Placement = pos=(0,0,3) rot=(0,0,1;0rad)
  Tip = -> Pad001
COMPONENT P35 — same part as P30; its construction recipe is shown at P30.
COMPONENT P36 — same part as P30; its construction recipe is shown at P30.
COMPONENT P37 — same part as P30; its construction recipe is shown at P30.
PROVENANCE & LICENSES
A FreeCAD (.FCStd) document from a public repository crawl; recipes are the document's own serialized feature recipes (and, for linked parts, companion documents' recipes).
License: cc0-1.0.
